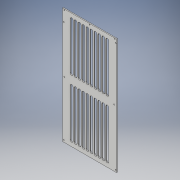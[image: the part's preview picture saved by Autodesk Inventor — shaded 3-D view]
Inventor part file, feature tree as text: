
AUTODESK INVENTOR PART (.ipt)
format: ipt  version: 2017 (Build 210142000, 142)  size: 271,360 bytes
history: native  units: in
note: dims shown in document units (in); Inventor stores cm internally (conversion verified against a paired STEP export)
features: sketch x4, extrude x3, hole x1
ambient origin geometry x8: Origin, YZ Plane, XZ Plane, XY Plane, X Axis, Y Axis, Z Axis, Center Point
bodies: Solid1 (feature_tree)
feature tree (8):
  extrude  "Extrusion1"  Depth=15.0in
  hole  "Hole1"  [1 undecoded]
  extrude  "Extrusion2"  Depth=1.5in
  extrude  "Extrusion3"  Depth=0.125in
  sketch  "Sketch1"  dims[d0=7.016in d1=15.0in]
  sketch  "Sketch2"  dims[d2=0.125in d3=0.0in d4=0.159in]
  sketch  "Sketch3"  dims[d5=0.25in d6=1.5in]
  sketch  "Sketch4"  dims[d7=90.0deg d8=0.125in d9=0.25in d10=0.125in d11=0.25in d12=0.14in d13=0.75in d14=0.375in d15=0.25in d16=0.5635in d17=1.0in d18=0.8108in d19=0.159in d21=0.125in d22=0.5in d23=0.125in d24=0.375in d34=0.5in d39=15.0in d40=6.0in d41=6.5in d44=3.937in d46=0.515in d47=0.3937in d49=1.0in d53=3.937in d55=0.515in d56=0.3937in d58=1.0in d60=1.0in d61=0.0in d63=6.5in d64=1.0in d65=1.0in d66=0.14in d68=0.14in d69=0.14in d70=0.0in d72=7.375in d74=3.258in d75=0.14in]
note: 1 required parameter value undecoded (feature->parameter linkage not recoverable at this tier; creation-order binding heuristic only, values carry confidence <= 0.55)
